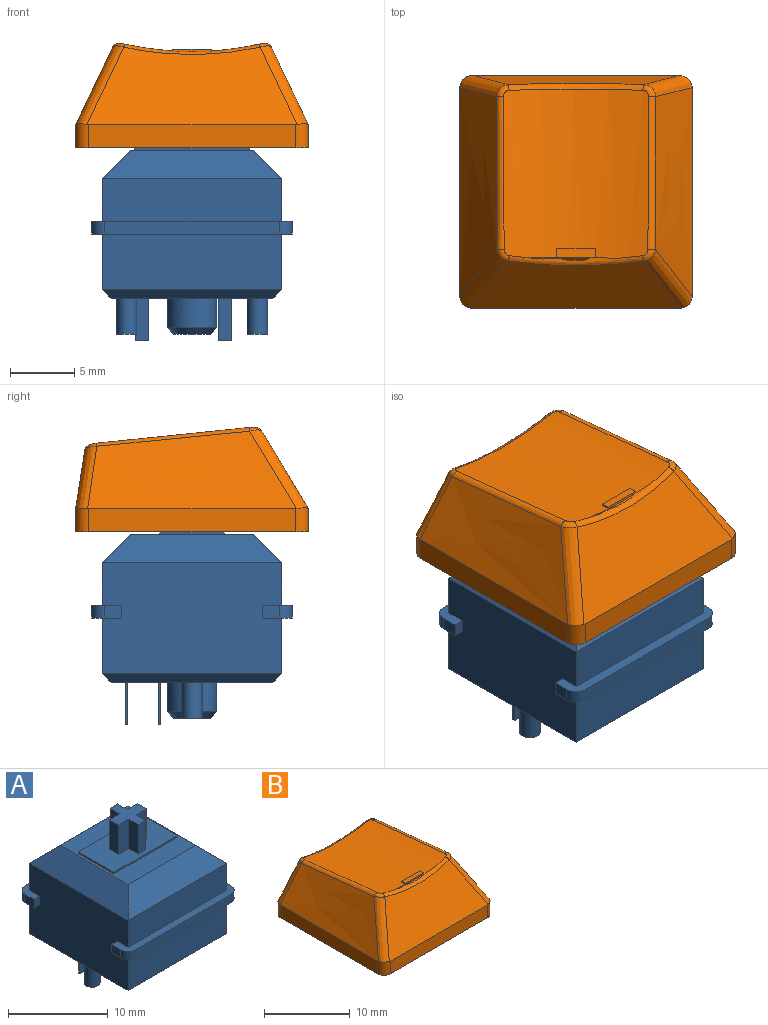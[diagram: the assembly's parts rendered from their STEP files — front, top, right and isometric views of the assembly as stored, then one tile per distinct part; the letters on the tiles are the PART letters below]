
ASSEMBLY  parts=2 mates=1
PART A: 69 faces, bbox 15.6x15.6x18.6 mm
  f0: plane 15.6x2.3mm, normal (0,0,-1), area 14.4mm2, adj f2,f3,f28,f30,f35,f60,f62,f63
  f1: plane 15.6x2.3mm, normal (0,0,-1), area 14.4mm2, adj f28,f30,f33,f34,f36,f59,f61,f64
  f2: plane 1.3x1mm, normal (1,0,0), area 1.3mm2, adj f0,f32,f62,f66
  f3: plane 1.3x1mm, normal (-1,0,0), area 1.3mm2, adj f0,f32,f63,f68
  f4: plane 15.6x2.3mm, normal (0,0,1), area 14.4mm2, adj f28,f30,f31,f33,f34,f36,f61,f64
  f5: plane 14x2.2mm, normal (-0.71,0,0.71), area 36.7mm2, adj f6,f7,f26,f30
  f6: plane 14x2.2mm, normal (0,-0.71,0.71), area 36.7mm2, adj f5,f7,f27,f31
  f7: plane 9.6x9.6mm, normal (0,0,1), area 47.2mm2, adj f5,f6,f8,f9,f10,f11,f26,f27
  f8: plane 5x0.2mm, normal (1,0,0), area 1mm2, adj f7,f9,f11,f12
  f9: plane 9x0.2mm, normal (0,1,0), area 1.8mm2, adj f7,f8,f10,f12
  f10: plane 5x0.2mm, normal (-1,0,0), area 1mm2, adj f7,f9,f11,f12
  f11: plane 9x0.2mm, normal (0,-1,0), area 1.8mm2, adj f7,f8,f10,f12
  f12: plane 9x5mm, normal (0,0,1), area 36.9mm2, adj f8,f9,f10,f11,f13,f14,f15,f16
  f13: plane 3.6x1.35mm, normal (1,0,0), area 4.9mm2, adj f12,f14,f24,f25
  f14: plane 3.6x1.08mm, normal (0,1,0), area 3.9mm2, adj f12,f13,f15,f25
  f15: plane 3.6x1.35mm, normal (-1,0,0), area 4.9mm2, adj f12,f14,f16,f25
  f16: plane 3.6x1.46mm, normal (0,1,0), area 5.3mm2, adj f12,f15,f17,f25
  f17: plane 3.6x1.3mm, normal (-1,0,0), area 4.7mm2, adj f12,f16,f18,f25
  f18: plane 3.6x1.46mm, normal (0,-1,0), area 5.3mm2, adj f12,f17,f19,f25
  f19: plane 3.6x1.35mm, normal (-1,0,0), area 4.9mm2, adj f12,f18,f20,f25
  f20: plane 3.6x1.08mm, normal (0,-1,0), area 3.9mm2, adj f12,f19,f21,f25
  f21: plane 3.6x1.35mm, normal (1,0,0), area 4.9mm2, adj f12,f20,f22,f25
  f22: plane 3.6x1.46mm, normal (0,-1,0), area 5.3mm2, adj f12,f21,f23,f25
  f23: plane 3.6x1.3mm, normal (1,0,0), area 4.7mm2, adj f12,f22,f24,f25
  f24: plane 3.6x1.46mm, normal (0,1,0), area 5.3mm2, adj f12,f13,f23,f25
  f25: plane 4x4mm, normal (0,0,1), area 8.1mm2, adj f13,f14,f15,f16,f17,f18,f19,f20
  f26: plane 14x2.2mm, normal (0,0.71,0.71), area 36.7mm2, adj f5,f7,f27,f29
  f27: plane 14x2.2mm, normal (0.71,0,0.71), area 36.7mm2, adj f6,f7,f26,f28
  f28: plane 14x8.6mm, normal (1,0,0), area 117.4mm2, adj f0,f1,f4,f27,f29,f31,f32,f55
  f29: plane 14x3.3mm, normal (0,1,0), area 46.2mm2, adj f26,f28,f30,f32
  f30: plane 14x8.6mm, normal (-1,0,0), area 117.4mm2, adj f0,f1,f4,f5,f29,f31,f32,f57
  f31: plane 14x3.3mm, normal (0,-1,0), area 46.2mm2, adj f4,f6,f28,f30
  f32: plane 15.6x2.3mm, normal (0,0,1), area 14.4mm2, adj f2,f3,f28,f29,f30,f35,f62,f63
  f33: plane 13.6x1mm, normal (0,-1,0), area 13.6mm2, adj f1,f4,f61,f64
  f34: plane 1.3x1mm, normal (1,0,0), area 1.3mm2, adj f1,f4,f61,f65
  f35: plane 13.6x1mm, normal (0,1,0), area 13.6mm2, adj f0,f32,f62,f63
  f36: plane 1.3x1mm, normal (-1,0,0), area 1.3mm2, adj f1,f4,f64,f67
  f37: plane 2.85x2.85mm, normal (0,0,-1), area 6.4mm2, adj f38
  f38: cone r=1.43mm half-angle=45deg, axis (0,0,1), area 7.4mm2, adj f37,f43
  f39: plane 1x0.2mm, normal (0,0,-1), area 0.2mm2, adj f44,f45,f46,f47
  f40: plane 1x0.2mm, normal (0,0,-1), area 0.2mm2, adj f48,f49,f50,f51
  f41: plane 1.6x1.6mm, normal (0,0,-1), area 2mm2, adj f52
  f42: plane 1.6x1.6mm, normal (0,0,-1), area 2mm2, adj f53
  f43: cylinder r=1.93mm len=3.85mm, axis (0,0,1), area 27.8mm2, adj f38,f54
  f44: plane 3.3x0.2mm, normal (-1,0,0), area 0.7mm2, adj f39,f45,f47,f54
  f45: plane 3.3x1mm, normal (0,1,0), area 3.3mm2, adj f39,f44,f46,f54
  f46: plane 3.3x0.2mm, normal (1,0,0), area 0.7mm2, adj f39,f45,f47,f54
  f47: plane 3.3x1mm, normal (0,-1,0), area 3.3mm2, adj f39,f44,f46,f54
  f48: plane 3.3x0.2mm, normal (-1,0,0), area 0.7mm2, adj f40,f49,f51,f54
  f49: plane 3.3x1mm, normal (0,1,0), area 3.3mm2, adj f40,f48,f50,f54
  f50: plane 3.3x0.2mm, normal (1,0,0), area 0.7mm2, adj f40,f49,f51,f54
  f51: plane 3.3x1mm, normal (0,-1,0), area 3.3mm2, adj f40,f48,f50,f54
  f52: cylinder r=0.8mm len=2.8mm, axis (0,0,1), area 14.1mm2, adj f41,f54
  f53: cylinder r=0.8mm len=2.8mm, axis (0,0,1), area 14.1mm2, adj f42,f54
  f54: plane 12.6x12.6mm, normal (0,0,-1), area 142.7mm2, adj f43,f44,f45,f46,f47,f48,f49,f50
  f55: plane 14x0.7mm, normal (0.71,0,-0.71), area 13.2mm2, adj f28,f54,f56,f58
  f56: plane 14x0.7mm, normal (0,0.71,-0.71), area 13.2mm2, adj f54,f55,f57,f60
  f57: plane 14x0.7mm, normal (-0.71,0,-0.71), area 13.2mm2, adj f30,f54,f56,f58
  f58: plane 14x0.7mm, normal (0,-0.71,-0.71), area 13.2mm2, adj f54,f55,f57,f59
  f59: plane 14x4.3mm, normal (0,-1,0), area 60.2mm2, adj f1,f28,f30,f58
  f60: plane 14x4.3mm, normal (0,1,0), area 60.2mm2, adj f0,f28,f30,f56
  f61: cylinder r=1mm len=1mm, axis (0,0,-1), area 1.6mm2, adj f1,f4,f33,f34
  f62: cylinder r=1mm len=1mm, axis (0,0,1), area 1.6mm2, adj f0,f2,f32,f35
  f63: cylinder r=1mm len=1mm, axis (0,0,-1), area 1.6mm2, adj f0,f3,f32,f35
  f64: cylinder r=1mm len=1mm, axis (0,0,1), area 1.6mm2, adj f1,f4,f33,f36
  f65: plane 1x0.8mm, normal (0,1,0), area 0.8mm2, adj f1,f4,f28,f34
  f66: plane 1x0.8mm, normal (0,-1,0), area 0.8mm2, adj f0,f2,f28,f32
  f67: plane 1x0.8mm, normal (0,1,0), area 0.8mm2, adj f1,f4,f30,f36
  f68: plane 1x0.8mm, normal (0,-1,0), area 0.8mm2, adj f0,f3,f30,f32
PART B: 55 faces, bbox 21.2x21.9x10.6 mm
  f0: cylinder r=22.9mm len=13.02mm, axis (0,0.99,-0.1), area 144.3mm2, adj f18,f19,f20,f21,f22,f23,f24,f25
  f1: plane 18.1x18.1mm, normal (0,0,-1), area 67.5mm2, adj f2,f3,f4,f5,f10,f12,f14,f16
  f2: plane 16.1x1.8mm, normal (1,0,0), area 29mm2, adj f1,f9,f10,f16
  f3: plane 16.1x1.8mm, normal (0,1,0), area 29mm2, adj f1,f6,f14,f15,f16,f17
  f4: plane 16.1x1.8mm, normal (-1,0,0), area 29mm2, adj f1,f7,f12,f14
  f5: plane 16.1x1.8mm, normal (0,-1,0), area 29mm2, adj f1,f8,f10,f12
  f6: plane 15.96x4.53mm, normal (0,0.99,0.15), area 56.4mm2, adj f3,f15,f17,f20
  f7: bspline ~18.1x6.49mm, area 87.4mm2, adj f4,f12,f13,f14,f15,f19
  f8: plane 16.37x6.05mm, normal (0,-0.86,0.51), area 90.2mm2, adj f5,f10,f11,f12,f13,f23
  f9: bspline ~18.1x6.49mm, area 87.4mm2, adj f2,f10,f11,f16,f17,f24
  f10: cylinder r=1mm len=1.88mm, axis (0,0,-1), area 2.9mm2, adj f1,f2,f5,f8,f9,f11
  f11: bspline ~7.99x5.46mm, area 10.4mm2, adj f8,f9,f10,f25
  f12: cylinder r=1mm len=1.88mm, axis (0,0,1), area 2.9mm2, adj f1,f4,f5,f7,f8,f13
  f13: bspline ~8.01x5.47mm, area 10.4mm2, adj f7,f8,f12,f21
  f14: cylinder r=1mm len=1.8mm, axis (0,0,-1), area 2.8mm2, adj f1,f3,f4,f7,f15
  f15: bspline ~6.46x4.4mm, area 8.2mm2, adj f3,f6,f7,f14,f18
  f16: cylinder r=1mm len=1.8mm, axis (0,0,1), area 2.8mm2, adj f1,f2,f3,f9,f17
  f17: bspline ~6.45x4.39mm, area 8.2mm2, adj f3,f6,f9,f16,f22
  f18: bspline ~1.17x1.02mm, area 0.7mm2, adj f0,f15,f19,f20
  f19: bspline ~17.37x2.1mm, area 8mm2, adj f0,f7,f18,f21
  f20: bspline ~10.64x1.03mm, area 7mm2, adj f0,f6,f18,f22
  f21: bspline ~1.13x1.07mm, area 0.7mm2, adj f0,f13,f19,f23
  f22: bspline ~1.17x1mm, area 0.7mm2, adj f0,f17,f20,f24
  f23: bspline ~10.62x0.82mm, area 6mm2, adj f0,f8,f21,f25
  f24: bspline ~17.37x2.1mm, area 8mm2, adj f0,f9,f22,f25
  f25: bspline ~1.24x1.01mm, area 0.7mm2, adj f0,f11,f23,f24
  f26: plane 16.13x1.61mm, normal (-1,0,0), area 25mm2, adj f1,f27,f29,f32,f33
  f27: plane 16.1x1.72mm, normal (0,-1,0), area 27.7mm2, adj f1,f26,f28,f30,f31,f33
  f28: plane 16.13x1.61mm, normal (1,0,0), area 25mm2, adj f1,f27,f29,f31,f32
  f29: plane 16.1x1.52mm, normal (0,1,0), area 24.5mm2, adj f1,f26,f28,f32
  f30: plane 16.21x4.45mm, normal (0,-0.99,-0.15), area 51mm2, adj f27,f31,f33,f34
  f31: offset ~20.1x8.49mm, area 78.8mm2, adj f27,f28,f30,f32,f34
  f32: plane 16.68x6.12mm, normal (0,0.86,-0.51), area 82.2mm2, adj f26,f28,f29,f31,f33,f34
  f33: offset ~20.1x8.49mm, area 78.8mm2, adj f26,f27,f30,f32,f34
  f34: cylinder r=23.9mm len=12.22mm, axis (0,0.99,-0.1), area 111.1mm2, adj f30,f31,f32,f33,f46
  f35: plane 5.88x1.35mm, normal (-1,0,0), area 7.8mm2, adj f36,f44,f45,f49
  f36: plane 5.97x1.5mm, normal (0,-1,0), area 8.9mm2, adj f35,f37,f45,f49
  f37: plane 6.1x1.3mm, normal (-1,0,0), area 7.8mm2, adj f36,f38,f45,f49
  f38: plane 6.1x1.5mm, normal (0,1,0), area 9.1mm2, adj f37,f39,f45,f49
  f39: plane 6.16x1.35mm, normal (-1,0,0), area 8.2mm2, adj f38,f40,f45,f49
  f40: plane 6.16x1mm, normal (0,1,0), area 6.2mm2, adj f39,f41,f45,f49
  f41: plane 6.16x1.35mm, normal (1,0,0), area 8.2mm2, adj f40,f42,f45,f49
  f42: plane 6.1x1.5mm, normal (0,1,0), area 9.1mm2, adj f41,f43,f45,f49
  f43: plane 6.1x1.3mm, normal (1,0,0), area 7.8mm2, adj f42,f45,f47,f49
  f44: plane 5.74x1mm, normal (0,-1,0), area 5.7mm2, adj f35,f45,f48,f49
  f45: plane 5.5x5.5mm, normal (0,0,-1), area 15.9mm2, adj f35,f36,f37,f38,f39,f40,f41,f42
  f46: cylinder r=2.75mm len=6.11mm, axis (0,0,-1), area 105.5mm2, adj f34,f45
  f47: plane 5.97x1.5mm, normal (0,-1,0), area 8.9mm2, adj f43,f45,f48,f49
  f48: plane 5.88x1.35mm, normal (1,0,0), area 7.8mm2, adj f44,f45,f47,f49
  f49: cylinder r=23.9mm len=4.01mm, axis (0,0.99,-0.1), area 7.9mm2, adj f35,f36,f37,f38,f39,f40,f41,f42
  f50: plane 0.71x0.22mm, normal (1,0,0), area 0.1mm2, adj f0,f51,f53,f54
  f51: plane 3x0.2mm, normal (0,0.99,-0.1), area 0.6mm2, adj f0,f50,f52,f54
  f52: plane 0.71x0.22mm, normal (-1,0,0), area 0.1mm2, adj f0,f51,f53,f54
  f53: plane 3x0.2mm, normal (0,-0.99,0.1), area 0.6mm2, adj f0,f50,f52,f54
  f54: plane 3x0.7mm, normal (0,0.1,0.99), area 2.1mm2, adj f50,f51,f52,f53
PLACE A at identity fixed
PLACE B t=(0,0,11.7)mm
MATE fastened B.f46 <-> A.f38  axis (0,0,-1) through (0,0,11.7)mm
